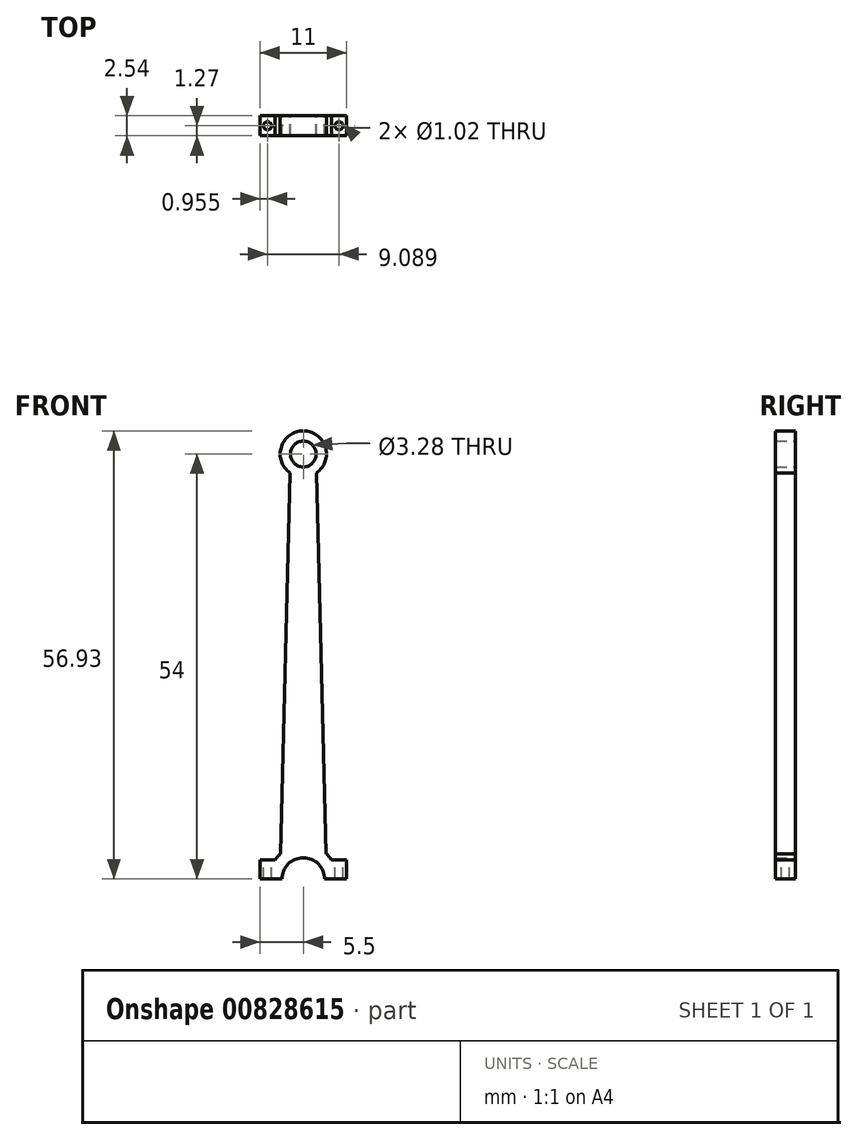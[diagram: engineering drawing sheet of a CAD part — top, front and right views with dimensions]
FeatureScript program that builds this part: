
annotation { "Feature Type Name" : "Feature", "Feature Type Description" : "" }
export const myFeature = defineFeature(function(context is Context, id is Id, definition is map)
    precondition{}
    {
        {
            var Q0;
            Q0=qCreatedBy(makeId("Front.planeOp"),FACE);
            var sketch = newSketch(context, id + "F0", { "sketchPlane" : qUnion([Q0])});
            skCircle(sketch, "E0", {"center": v(0, 0) * mm, "radius": 2.93 * mm});
            skCircle(sketch, "E1", {"center": v(0, 0) * mm, "radius": 1.64 * mm});
            skLineSegment(sketch, "E2", {"start": v(1.64, 0) * mm, "end": v(2.9, -50.78) * mm});
            skLineSegment(sketch, "E3.MirrorCS", {"start": v(-1.64, 0) * mm, "end": v(-2.9, -50.78) * mm});
            skCircle(sketch, "E4", {"center": v(0, -54) * mm, "radius": 4.33 * mm});
            skCircle(sketch, "E5", {"center": v(0, -54) * mm, "radius": 2.7 * mm});
            skLineSegment(sketch, "E6", {"start": v(0, -54) * mm, "end": v(4.33, -54) * mm});
            skLineSegment(sketch, "E7", {"start": v(4.33, -54) * mm, "end": v(-4.33, -54) * mm});
            skLineSegment(sketch, "E8.bottom", {"start": v(3.6, -54) * mm, "end": v(5.5, -54) * mm});
            skLineSegment(sketch, "E8.top", {"start": v(3.6, -51.55) * mm, "end": v(5.5, -51.55) * mm});
            skLineSegment(sketch, "E8.right", {"start": v(5.5, -54) * mm, "end": v(5.5, -51.55) * mm});
            skLineSegment(sketch, "E9.MirrorCS", {"start": v(-3.6, -51.55) * mm, "end": v(-5.5, -51.55) * mm});
            skLineSegment(sketch, "E10.MirrorCS", {"start": v(-5.5, -54) * mm, "end": v(-5.5, -51.55) * mm});
            skLineSegment(sketch, "E11.MirrorCS", {"start": v(-3.6, -54) * mm, "end": v(-5.5, -54) * mm});
            skLineSegment(sketch, "E12", {"start": v(3.6, -51.55) * mm, "end": v(3.6, -54) * mm});
            skLineSegment(sketch, "E13", {"start": v(-3.6, -51.55) * mm, "end": v(-3.6, -54) * mm});
            skSolve(sketch);
        }
        {
            var Q0;
            {var subQ0=sQuery(id+"F0.wireOp",EDGE,"E2");var subQ1=sQuery(id+"F0.wireOp",EDGE,"E0");var subQ2=makeQuery(id+"F0.imprint","INTERSECT",VERTEX,{"derivedFrom":[subQ1,subQ0]});Q0=makeQuery(id+"F0.imprint","IMPRINT",FACE,{"disambiguationData":[TD([[makeQuery(id+"F0.imprint","IMPRINT",EDGE,{"disambiguationData":[TD([[subQ2,1.0]])],"derivedFrom":subQ1}),-1.0]])]});}
            var Q1;
            {var subQ0=sQuery(id+"F0.wireOp",EDGE,"E2");var subQ1=sQuery(id+"F0.wireOp",EDGE,"E0");var subQ2=makeQuery(id+"F0.imprint","INTERSECT",VERTEX,{"derivedFrom":[subQ1,subQ0]});Q1=makeQuery(id+"F0.imprint","IMPRINT",FACE,{"disambiguationData":[TD([[makeQuery(id+"F0.imprint","IMPRINT",EDGE,{"disambiguationData":[TD([[subQ2,-1.0]])],"derivedFrom":subQ1}),1.0]])]});}
            var Q2;
            {var subQ0=sQuery(id+"F0.wireOp",EDGE,"E2");var subQ1=sQuery(id+"F0.wireOp",EDGE,"E0");var subQ2=makeQuery(id+"F0.imprint","INTERSECT",VERTEX,{"derivedFrom":[subQ1,subQ0]});Q2=makeQuery(id+"F0.imprint","IMPRINT",FACE,{"disambiguationData":[TD([[makeQuery(id+"F0.imprint","IMPRINT",EDGE,{"disambiguationData":[TD([[subQ2,1.0]])],"derivedFrom":subQ1}),1.0]])]});}
            var Q3;
            {var subQ1=sQuery(id+"F0.wireOp",EDGE,"E4");var subQ10=sQuery(id+"F0.wireOp",EDGE,"E12");var subQ11=makeQuery(id+"F0.imprint","INTERSECT",VERTEX,{"derivedFrom":[subQ1,subQ10]});Q3=makeQuery(id+"F0.imprint","IMPRINT",FACE,{"disambiguationData":[TD([[makeQuery(id+"F0.imprint","IMPRINT",EDGE,{"disambiguationData":[TD([[subQ11,-1.0]])],"derivedFrom":subQ1}),1.0]])]});}
            var Q4;
            {var subQ1=sQuery(id+"F0.wireOp",EDGE,"E4");var subQ3=sQuery(id+"F0.wireOp",EDGE,"E12");var subQ4=makeQuery(id+"F0.imprint","INTERSECT",VERTEX,{"derivedFrom":[subQ1,subQ3]});Q4=makeQuery(id+"F0.imprint","IMPRINT",FACE,{"disambiguationData":[TD([[makeQuery(id+"F0.imprint","IMPRINT",EDGE,{"disambiguationData":[TD([[subQ4,-1.0]])],"derivedFrom":subQ3}),1.0]])]});}
            var Q5;
            {var subQ0=sQuery(id+"F0.wireOp",EDGE,"E8.bottom");Q5=makeQuery(id+"F0.imprint","IMPRINT",FACE,{"disambiguationData":[TD([[makeQuery(id+"F0.imprint","IMPRINT",EDGE,{"derivedFrom":subQ0}),1.0]])]});}
            var Q6;
            {var subQ1=sQuery(id+"F0.wireOp",EDGE,"E4");var subQ3=sQuery(id+"F0.wireOp",EDGE,"E13");var subQ4=makeQuery(id+"F0.imprint","INTERSECT",VERTEX,{"derivedFrom":[subQ1,subQ3]});Q6=makeQuery(id+"F0.imprint","IMPRINT",FACE,{"disambiguationData":[TD([[makeQuery(id+"F0.imprint","IMPRINT",EDGE,{"disambiguationData":[TD([[subQ4,-1.0]])],"derivedFrom":subQ3}),-1.0]])]});}
            var Q7;
            {var subQ0=sQuery(id+"F0.wireOp",EDGE,"E9.MirrorCS");Q7=makeQuery(id+"F0.imprint","IMPRINT",FACE,{"disambiguationData":[TD([[makeQuery(id+"F0.imprint","IMPRINT",EDGE,{"derivedFrom":subQ0}),1.0]])]});}
            extrude(context, id + "F1", {"entities" : qUnion([Q0, Q1, Q2, Q3, Q4, Q5, Q6, Q7]), "endBound" : BoundingType.SYMMETRIC, "depth" : 2.54 * mm, "offsetDistance" : 25.4 * mm});
        }
        {
            var Q0;
            {var subQ0=sQuery(id+"F0.wireOp",EDGE,"E2");var subQ1=sQuery(id+"F0.wireOp",EDGE,"E0");var subQ2=makeQuery(id+"F0.imprint","INTERSECT",VERTEX,{"derivedFrom":[subQ1,subQ0]});Q0=makeQuery(id+"F0.imprint","IMPRINT",FACE,{"disambiguationData":[TD([[makeQuery(id+"F0.imprint","IMPRINT",EDGE,{"disambiguationData":[TD([[subQ2,1.0]])],"derivedFrom":subQ1}),-1.0]])]});}
            var Q1;
            {var subQ0=sQuery(id+"F0.wireOp",EDGE,"E2");var subQ1=sQuery(id+"F0.wireOp",EDGE,"E0");var subQ2=makeQuery(id+"F0.imprint","INTERSECT",VERTEX,{"derivedFrom":[subQ1,subQ0]});Q1=makeQuery(id+"F0.imprint","IMPRINT",FACE,{"disambiguationData":[TD([[makeQuery(id+"F0.imprint","IMPRINT",EDGE,{"disambiguationData":[TD([[subQ2,-1.0]])],"derivedFrom":subQ1}),1.0]])]});}
            var Q2;
            {var subQ0=sQuery(id+"F0.wireOp",EDGE,"E2");var subQ1=sQuery(id+"F0.wireOp",EDGE,"E0");var subQ2=makeQuery(id+"F0.imprint","INTERSECT",VERTEX,{"derivedFrom":[subQ1,subQ0]});Q2=makeQuery(id+"F0.imprint","IMPRINT",FACE,{"disambiguationData":[TD([[makeQuery(id+"F0.imprint","IMPRINT",EDGE,{"disambiguationData":[TD([[subQ2,1.0]])],"derivedFrom":subQ1}),1.0]])]});}
            var Q3;
            {var subQ1=sQuery(id+"F0.wireOp",EDGE,"E4");var subQ10=sQuery(id+"F0.wireOp",EDGE,"E12");var subQ11=makeQuery(id+"F0.imprint","INTERSECT",VERTEX,{"derivedFrom":[subQ1,subQ10]});Q3=makeQuery(id+"F0.imprint","IMPRINT",FACE,{"disambiguationData":[TD([[makeQuery(id+"F0.imprint","IMPRINT",EDGE,{"disambiguationData":[TD([[subQ11,-1.0]])],"derivedFrom":subQ1}),1.0]])]});}
            extrude(context, id + "F2", {"entities" : qUnion([Q0, Q1, Q2, Q3]), "operationType" : NewBodyOperationType.ADD, "endBound" : BoundingType.SYMMETRIC, "depth" : 2.54 * mm, "offsetDistance" : 25.4 * mm});
        }
        {
            var Q0;
            Q0=makeQuery(id+"F1.opExtrude","SWEPT_FACE",FACE,{"disambiguationData":[OSD([sQuery(id+"F0.wireOp",EDGE,"E9.MirrorCS")])]});
            var sketch = newSketch(context, id + "F3", { "sketchPlane" : qUnion([Q0])});
            skCircle(sketch, "E14", {"center": v(-4.54, 0) * mm, "radius": 0.5 * mm});
            skSolve(sketch);
        }
        {
            var Q0;
            Q0=makeQuery(id+"F1.opExtrude","SWEPT_FACE",FACE,{"disambiguationData":[OSD([sQuery(id+"F0.wireOp",EDGE,"E8.top")])]});
            var sketch = newSketch(context, id + "F4", { "sketchPlane" : qUnion([Q0])});
            skCircle(sketch, "E15", {"center": v(4.54, 0) * mm, "radius": 0.5 * mm});
            skSolve(sketch);
        }
        {
            var Q0;
            Q0=makeQuery(id+"F3.imprint","IMPRINT",FACE,{"disambiguationData":[TD([[makeQuery(id+"F3.imprint","IMPRINT",EDGE,{"derivedFrom":sQuery(id+"F3.wireOp",EDGE,"E14")}),1.0]])]});
            var Q1;
            Q1=makeQuery(id+"F4.imprint","IMPRINT",FACE,{"disambiguationData":[TD([[makeQuery(id+"F4.imprint","IMPRINT",EDGE,{"derivedFrom":sQuery(id+"F4.wireOp",EDGE,"E15")}),1.0]])]});
            extrude(context, id + "F5", {"entities" : qUnion([Q0, Q1]), "operationType" : NewBodyOperationType.REMOVE, "oppositeDirection" : true, "depth" : 25.4 * mm, "offsetDistance" : 25.4 * mm});
        }
    });
